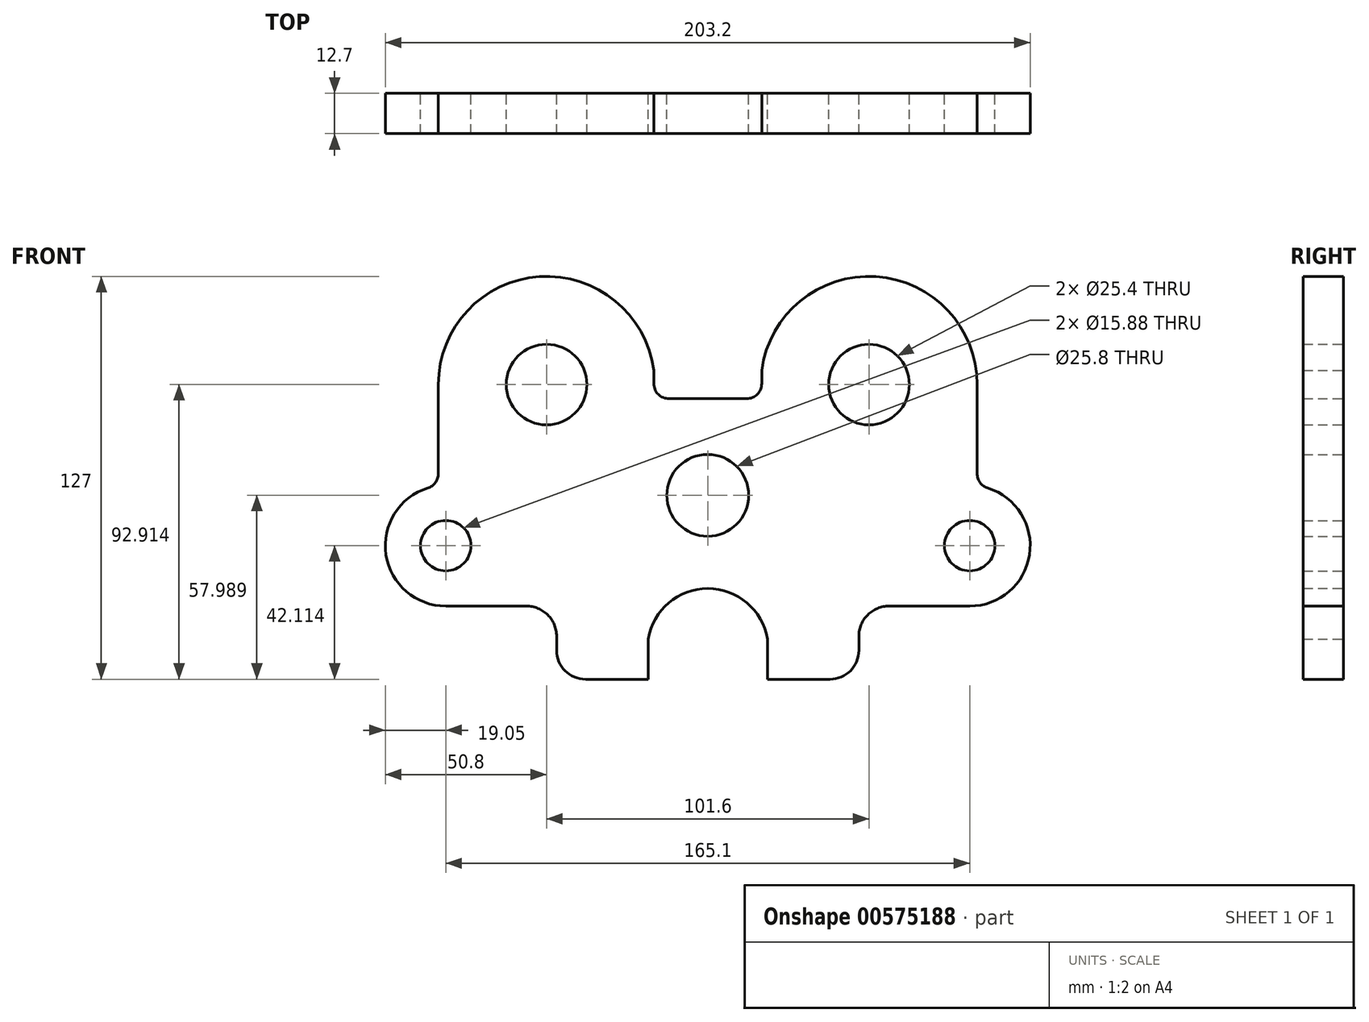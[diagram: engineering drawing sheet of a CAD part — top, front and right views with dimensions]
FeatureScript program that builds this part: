
annotation { "Feature Type Name" : "Feature", "Feature Type Description" : "" }
export const myFeature = defineFeature(function(context is Context, id is Id, definition is map)
    precondition{}
    {
        {
            var Q0;
            Q0=qCreatedBy(makeId("Front.planeOp"),FACE);
            var sketch = newSketch(context, id + "F0", { "sketchPlane" : qUnion([Q0])});
            skArc(sketch, "E0.MirrorCS", {"start": v(17, 52.22) * mm, "mid": v(53.03, 81.78) * mm, "end": v(84.89, 47.76) * mm});
            skLineSegment(sketch, "E1", {"start": v(84.89, 47.76) * mm, "end": v(84.89, 19.7) * mm});
            skCircle(sketch, "E2", {"center": v(50.8, 47.76) * mm, "radius": 12.7 * mm});
            skLineSegment(sketch, "E3", {"start": v(47.62, -31.6) * mm, "end": v(47.62, -36.03) * mm});
            skLineSegment(sketch, "E4", {"start": v(57.15, -22.08) * mm, "end": v(82.55, -22.09) * mm});
            skLineSegment(sketch, "E5", {"start": v(38.5, -45.15) * mm, "end": v(18.8, -45.15) * mm});
            skLineSegment(sketch, "E6", {"start": v(0, 82.43) * mm, "end": v(0, -73.32) * mm, "construction": true});
            skArc(sketch, "E7", {"start": v(82.55, -22.09) * mm, "mid": v(101.38, -5.92) * mm, "end": v(88.24, 15.14) * mm});
            skCircle(sketch, "E8", {"center": v(82.55, -3.04) * mm, "radius": 6.35 * mm});
            skCircle(sketch, "E9", {"center": v(0, 12.84) * mm, "radius": 12.9 * mm});
            skPoint(sketch, "E10.visualSharp", {"position": v(47.62, -22.08) * mm});
            skArc(sketch, "E10.filletArc", {"start": v(57.15, -22.08) * mm, "mid": v(50.4, -24.87) * mm, "end": v(47.62, -31.6) * mm});
            skPoint(sketch, "E11.visualSharp", {"position": v(47.62, -45.15) * mm});
            skArc(sketch, "E11.filletArc", {"start": v(38.5, -45.15) * mm, "mid": v(44.95, -42.48) * mm, "end": v(47.62, -36.03) * mm});
            skPoint(sketch, "E12.visualSharp", {"position": v(84.89, 15.87) * mm});
            skArc(sketch, "E12.filletArc", {"start": v(84.89, 19.7) * mm, "mid": v(85.82, 16.87) * mm, "end": v(88.24, 15.14) * mm});
            skLineSegment(sketch, "E13", {"start": v(-38.81, 12.84) * mm, "end": v(37.58, 12.82) * mm, "construction": true});
            skLineSegment(sketch, "E14", {"start": v(29.1, 47.76) * mm, "end": v(72.42, 47.76) * mm, "construction": true});
            skLineSegment(sketch, "E15", {"start": v(50.8, 71.2) * mm, "end": v(50.8, 24.74) * mm, "construction": true});
            skLineSegment(sketch, "E16", {"start": v(58.48, -3.04) * mm, "end": v(97.34, -3.04) * mm, "construction": true});
            skLineSegment(sketch, "E17", {"start": v(-27.2, -27.38) * mm, "end": v(26.4, -27.4) * mm, "construction": true});
            skLineSegment(sketch, "E18", {"start": v(82.55, 11.19) * mm, "end": v(82.55, -41.53) * mm, "construction": true});
            skLineSegment(sketch, "E19", {"start": v(17, 52.22) * mm, "end": v(17, 48.07) * mm});
            skLineSegment(sketch, "E20.MirrorCS", {"start": v(-17, 52.22) * mm, "end": v(-17, 48.07) * mm});
            skArc(sketch, "E21.MirrorCS", {"start": v(-17, 52.22) * mm, "mid": v(-53.03, 81.78) * mm, "end": v(-84.89, 47.76) * mm});
            skLineSegment(sketch, "E22.MirrorCS", {"start": v(-84.89, 47.76) * mm, "end": v(-84.89, 19.7) * mm});
            skArc(sketch, "E23.MirrorCS", {"start": v(-84.89, 19.7) * mm, "mid": v(-85.82, 16.87) * mm, "end": v(-88.24, 15.14) * mm});
            skArc(sketch, "E24.MirrorCS", {"start": v(-82.55, -22.09) * mm, "mid": v(-101.38, -5.92) * mm, "end": v(-88.24, 15.14) * mm});
            skLineSegment(sketch, "E25.MirrorCS", {"start": v(-57.15, -22.08) * mm, "end": v(-82.55, -22.09) * mm});
            skArc(sketch, "E26.MirrorCS", {"start": v(-57.15, -22.08) * mm, "mid": v(-50.4, -24.87) * mm, "end": v(-47.62, -31.6) * mm});
            skLineSegment(sketch, "E27.MirrorCS", {"start": v(-47.62, -31.6) * mm, "end": v(-47.62, -36.03) * mm});
            skArc(sketch, "E28.MirrorCS", {"start": v(-38.5, -45.15) * mm, "mid": v(-44.95, -42.48) * mm, "end": v(-47.62, -36.03) * mm});
            skLineSegment(sketch, "E29.MirrorCS", {"start": v(-38.5, -45.15) * mm, "end": v(-18.8, -45.15) * mm});
            skLineSegment(sketch, "E30", {"start": v(-12.23, 43.3) * mm, "end": v(12.23, 43.3) * mm});
            skLineSegment(sketch, "E31", {"start": v(-18.8, -45.15) * mm, "end": v(-18.8, -32.45) * mm});
            skLineSegment(sketch, "E32", {"start": v(18.8, -45.15) * mm, "end": v(18.8, -32.45) * mm});
            skArc(sketch, "E33", {"start": v(18.8, -32.45) * mm, "mid": v(0, -16.53) * mm, "end": v(-18.8, -32.45) * mm});
            skCircle(sketch, "E34.MirrorC", {"center": v(-50.8, 47.76) * mm, "radius": 12.7 * mm});
            skCircle(sketch, "E35.MirrorC", {"center": v(-82.55, -3.04) * mm, "radius": 6.35 * mm});
            skPoint(sketch, "E36.visualSharp", {"position": v(17, 43.3) * mm});
            skArc(sketch, "E36.filletArc", {"start": v(12.23, 43.3) * mm, "mid": v(15.6, 44.7) * mm, "end": v(17, 48.07) * mm});
            skPoint(sketch, "E37.visualSharp", {"position": v(-17, 43.3) * mm});
            skArc(sketch, "E37.filletArc", {"start": v(-17, 48.07) * mm, "mid": v(-15.6, 44.7) * mm, "end": v(-12.23, 43.3) * mm});
            skCircle(sketch, "E38", {"center": v(-82.55, -3.04) * mm, "radius": 7.94 * mm});
            skCircle(sketch, "E39", {"center": v(82.55, -3.04) * mm, "radius": 7.94 * mm});
            skSolve(sketch);
        }
        {
            var Q0;
            Q0=qSketchRegion(id+"F0",true);
            extrude(context, id + "F1", {"entities" : qUnion([Q0]), "depth" : 12.7 * mm, "offsetDistance" : 25.4 * mm});
        }
    });
